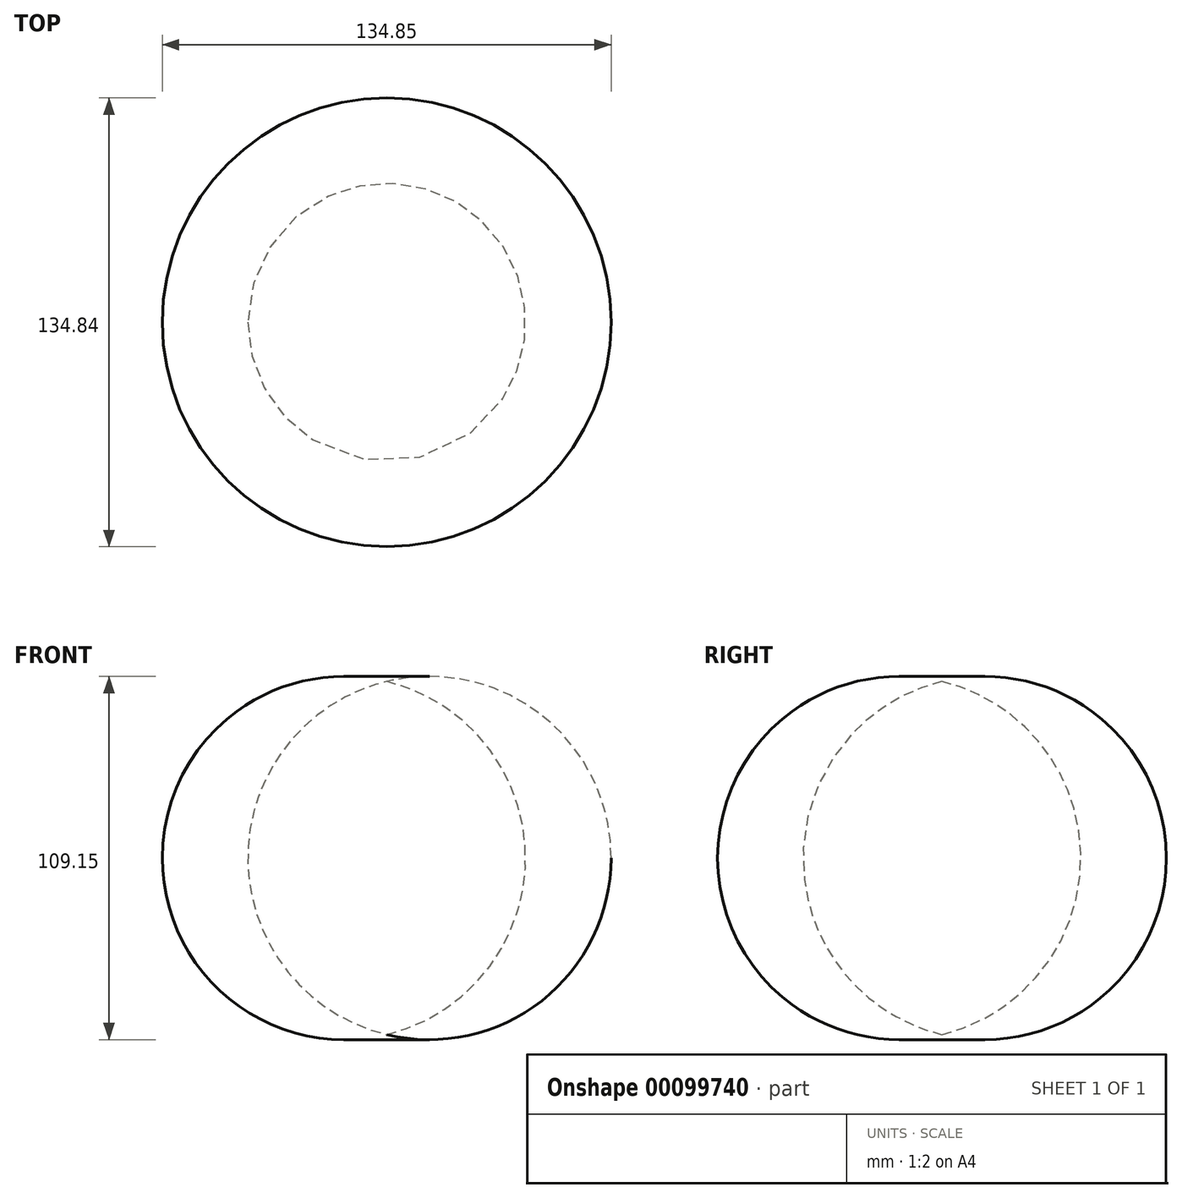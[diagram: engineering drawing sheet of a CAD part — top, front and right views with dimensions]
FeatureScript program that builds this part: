
annotation { "Feature Type Name" : "Feature", "Feature Type Description" : "" }
export const myFeature = defineFeature(function(context is Context, id is Id, definition is map)
    precondition{}
    {
        {
            var Q0;
            Q0=qCreatedBy(makeId("Front.planeOp"),FACE);
            var sketch = newSketch(context, id + "F0", { "sketchPlane" : qUnion([Q0])});
            skLineSegment(sketch, "E0", {"start": v(-42.61, 54.08) * mm, "end": v(-42.61, -52) * mm});
            skArc(sketch, "E1", {"start": v(-42.61, -52) * mm, "mid": v(-0.88, 1.04) * mm, "end": v(-42.61, 54.08) * mm});
            skSolve(sketch);
        }
        {
            var Q0;
            Q0=makeQuery(id+"F0.imprint","IMPRINT",FACE,{"disambiguationData":[TD([[makeQuery(id+"F0.imprint","IMPRINT",EDGE,{"derivedFrom":sQuery(id+"F0.wireOp",EDGE,"E0")}),1.0]])]});
            var Q1;
            Q1=sQuery(id+"F0.wireOp",EDGE,"E0");
            revolve(context, id + "F1", {"entities" : qUnion([Q0]), "axis" : qUnion([Q1]), "revolveType" : RevolveType.FULL});
        }
    });
